# Revit family: Grille-Supply-Carnes-RADM-Extruded-Aluminum
name_source: partatom
category: Duct Accessories
revit_build: Autodesk Revit MEP 2014 (Build: 20130308_1515(x64)
units: mm (PartAtom-declared; Revit-internal decimal feet)

## types (1)
- Parametric
    # Of Blades in Verticle = 2
    #o Of Blades in Horizonta = 5
    Blade Spacing = 3/4"
    Catalog = http://www.carnes.com
    Default Elevation = 0"
    Depth = 4"
    Description = Square and Rectangular Registers and Grilles
    Diffuser Plate = Metal - Carnes - Extruded-Aluminum
    Duct Height = 4"
    Duct Width = 2"
    Flow = 0 CFM
    Height = 1 7/8"
    Inner Depth = 1 1/2"
    Inner Width = 3 1/2"
    Manufacturer = CARNES COMPANY
    Model = RADM
    Product Page URL = http://www.carnes.com
    Revit Object Download Link = http://library.smartbim.com
    Specification Sheet = http://www.carnes.com
    Subcatagory = Air Distribution
    Supply Connection = Diffuser Supply Connector
    Supply Connector = Yes
    URL = http://www.carnes.com
    Unit = Metal - Carnes - Extruded-Aluminum
    Width = 6"

## geometry (parser evidence)
native form markers: Sweep x8
no freeform markers — native parametric forms only
